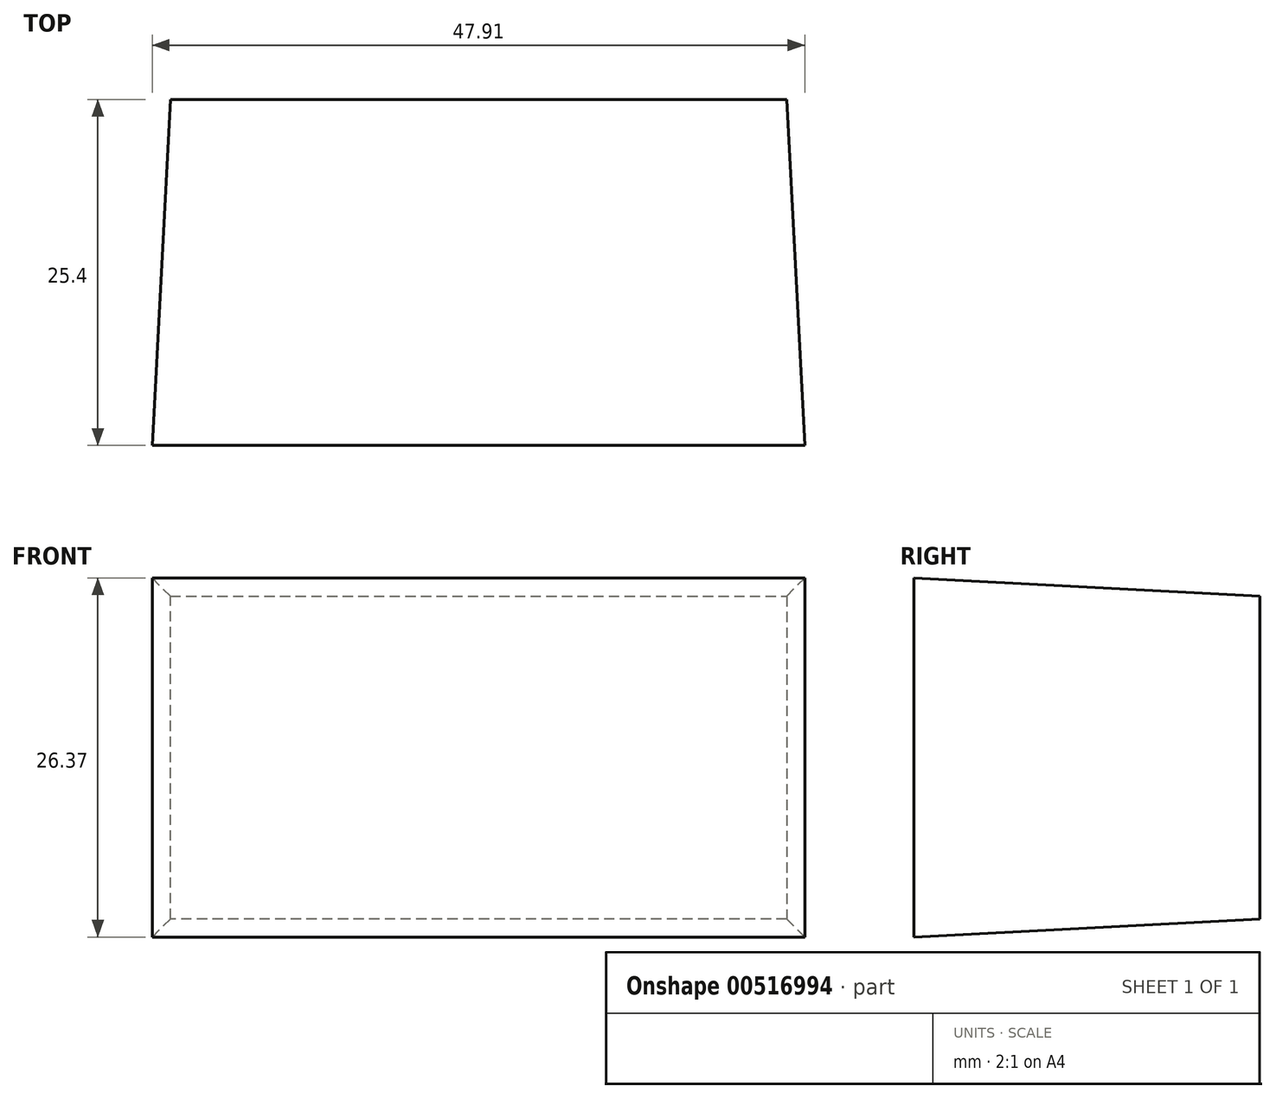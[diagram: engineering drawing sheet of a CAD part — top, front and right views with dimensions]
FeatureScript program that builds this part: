
annotation { "Feature Type Name" : "Feature", "Feature Type Description" : "" }
export const myFeature = defineFeature(function(context is Context, id is Id, definition is map)
    precondition{}
    {
        {
            var Q0;
            Q0=qCreatedBy(makeId("Front.planeOp"),FACE);
            var sketch = newSketch(context, id + "F0", { "sketchPlane" : qUnion([Q0])});
            skLineSegment(sketch, "E0.bottom", {"start": v(-51.62, 37.11) * mm, "end": v(-6.37, 37.11) * mm});
            skLineSegment(sketch, "E0.top", {"start": v(-51.62, 60.81) * mm, "end": v(-6.37, 60.81) * mm});
            skLineSegment(sketch, "E0.left", {"start": v(-51.62, 37.11) * mm, "end": v(-51.62, 60.81) * mm});
            skLineSegment(sketch, "E0.right", {"start": v(-6.37, 37.11) * mm, "end": v(-6.37, 60.81) * mm});
            skSolve(sketch);
        }
        {
            var Q0;
            Q0 = qSketchRegion(id + "F0", true);
            extrude(context, id + "F1", {"entities" : qUnion([Q0]), "depth" : 25.4 * mm, "offsetDistance" : 25.4 * mm, "hasDraft" : true, "draftAngle" : 3 * degree});
        }
    });
